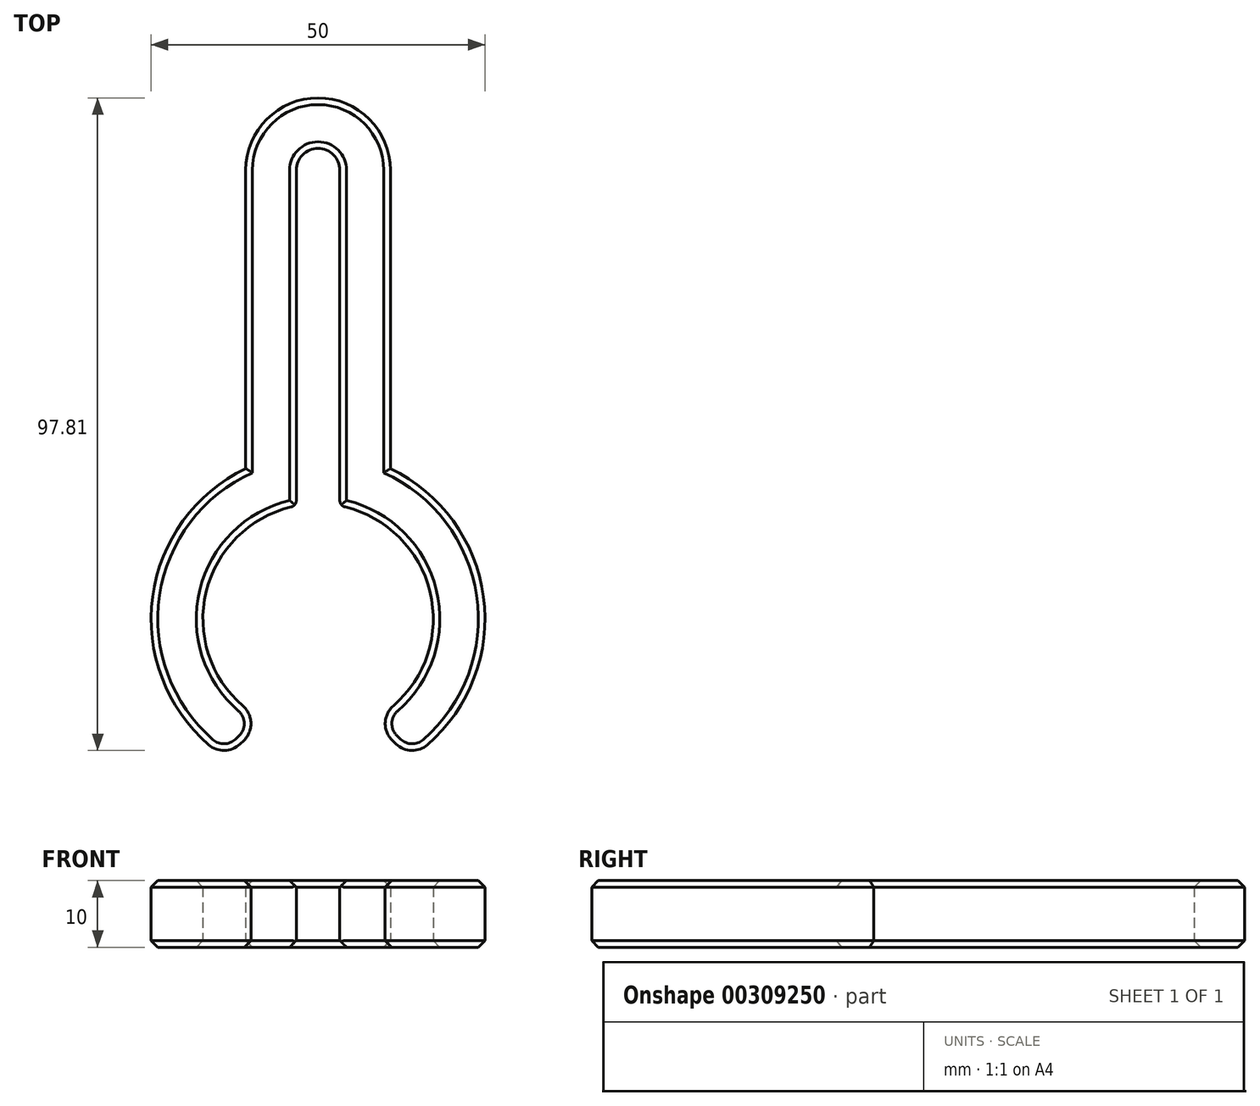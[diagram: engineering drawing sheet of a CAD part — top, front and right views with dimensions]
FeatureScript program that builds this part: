
annotation { "Feature Type Name" : "Feature", "Feature Type Description" : "" }
export const myFeature = defineFeature(function(context is Context, id is Id, definition is map)
    precondition{}
    {
        {
            var Q0;
            Q0=qCreatedBy(makeId("Top.planeOp"),FACE);
            var sketch = newSketch(context, id + "F0", { "sketchPlane" : qUnion([Q0])});
            skArc(sketch, "E0", {"start": v(-39.63, 17.45) * mm, "mid": v(-53.44, 3.03) * mm, "end": v(-44.38, -14.76) * mm});
            skArc(sketch, "E1", {"start": v(-47.2, 23.05) * mm, "mid": v(-61.31, 2.25) * mm, "end": v(-50.22, -20.3) * mm});
            skArc(sketch, "E2", {"start": v(-33.11, 67.76) * mm, "mid": v(-36.37, 71.03) * mm, "end": v(-39.63, 67.76) * mm});
            skArc(sketch, "E3", {"start": v(-25.54, 67.76) * mm, "mid": v(-36.37, 78.6) * mm, "end": v(-47.2, 67.76) * mm});
            skLineSegment(sketch, "E4", {"start": v(-25.54, 67.76) * mm, "end": v(-25.54, 23.05) * mm});
            skLineSegment(sketch, "E5", {"start": v(-47.2, 67.76) * mm, "end": v(-47.2, 23.05) * mm});
            skLineSegment(sketch, "E6", {"start": v(-33.11, 67.76) * mm, "end": v(-33.11, 17.45) * mm});
            skLineSegment(sketch, "E7", {"start": v(-39.63, 67.76) * mm, "end": v(-39.63, 17.45) * mm});
            skArc(sketch, "E8.trimOffspring", {"start": v(-28.36, -14.76) * mm, "mid": v(-19.3, 3.03) * mm, "end": v(-33.11, 17.45) * mm});
            skArc(sketch, "E9.trimOffspring", {"start": v(-22.52, -20.3) * mm, "mid": v(-11.43, 2.25) * mm, "end": v(-25.54, 23.05) * mm});
            skLineSegment(sketch, "E10", {"start": v(-50.22, -20.3) * mm, "end": v(-44.38, -14.76) * mm});
            skLineSegment(sketch, "E11", {"start": v(-28.36, -14.76) * mm, "end": v(-22.52, -20.3) * mm});
            skSolve(sketch);
        }
        {
            var Q0;
            Q0 = qSketchRegion(id + "F0", true);
            extrude(context, id + "F1", {"entities" : qUnion([Q0]), "depth" : 10 * mm});
        }
        {
            var Q0;
            Q0=makeQuery(id+"F1.opExtrude","SWEPT_EDGE",EDGE,{"disambiguationData":[OSD([sQuery(id+"F0.wireOp",EDGE,"E1"),sQuery(id+"F0.wireOp",EDGE,"E10")])]});
            var Q1;
            Q1=makeQuery(id+"F1.opExtrude","SWEPT_EDGE",EDGE,{"disambiguationData":[OSD([sQuery(id+"F0.wireOp",EDGE,"E0"),sQuery(id+"F0.wireOp",EDGE,"E10")])]});
            var Q2;
            Q2=makeQuery(id+"F1.opExtrude","SWEPT_EDGE",EDGE,{"disambiguationData":[OSD([sQuery(id+"F0.wireOp",EDGE,"E8.trimOffspring"),sQuery(id+"F0.wireOp",EDGE,"E11")])]});
            var Q3;
            Q3=makeQuery(id+"F1.opExtrude","SWEPT_EDGE",EDGE,{"disambiguationData":[OSD([sQuery(id+"F0.wireOp",EDGE,"E9.trimOffspring"),sQuery(id+"F0.wireOp",EDGE,"E11")])]});
            fillet(context, id + "F2", {"entities" : qUnion([Q0, Q1, Q2, Q3]), "radius" : 3.5 * mm, "tangentPropagation" : true, "allowEdgeOverflow" : false});
        }
        {
            var Q0;
            Q0=makeQuery(id+"F1.opExtrude","CAP_EDGE",EDGE,{"disambiguationData":[OSD([sQuery(id+"F0.wireOp",EDGE,"E0")])],"isStart":false});
            var Q1;
            Q1=makeQuery(id+"F1.opExtrude","CAP_EDGE",EDGE,{"disambiguationData":[OSD([sQuery(id+"F0.wireOp",EDGE,"leTiJdDx-6Tv0-o62X-Sqed-6rVeZV9HhB44")])],"isStart":false});
            var Q2;
            Q2=makeQuery(id+"F1.opExtrude","CAP_EDGE",EDGE,{"disambiguationData":[OSD([sQuery(id+"F0.wireOp",EDGE,"E1")])],"isStart":false});
            var Q3;
            Q3=makeQuery(id+"F1.opExtrude","CAP_EDGE",EDGE,{"disambiguationData":[OSD([sQuery(id+"F0.wireOp",EDGE,"E5")])],"isStart":false});
            var Q4;
            Q4=makeQuery(id+"F1.opExtrude","CAP_EDGE",EDGE,{"disambiguationData":[OSD([sQuery(id+"F0.wireOp",EDGE,"E7")])],"isStart":false});
            var Q5;
            Q5=makeQuery(id+"F1.opExtrude","CAP_EDGE",EDGE,{"disambiguationData":[OSD([sQuery(id+"F0.wireOp",EDGE,"E3")])],"isStart":false});
            var Q6;
            Q6=makeQuery(id+"F1.opExtrude","CAP_EDGE",EDGE,{"disambiguationData":[OSD([sQuery(id+"F0.wireOp",EDGE,"E2")])],"isStart":false});
            var Q7;
            Q7=makeQuery(id+"F1.opExtrude","CAP_EDGE",EDGE,{"disambiguationData":[OSD([sQuery(id+"F0.wireOp",EDGE,"E6")])],"isStart":false});
            var Q8;
            Q8=makeQuery(id+"F1.opExtrude","CAP_EDGE",EDGE,{"disambiguationData":[OSD([sQuery(id+"F0.wireOp",EDGE,"E4")])],"isStart":false});
            var Q9;
            Q9=makeQuery(id+"F1.opExtrude","CAP_EDGE",EDGE,{"disambiguationData":[OSD([sQuery(id+"F0.wireOp",EDGE,"E8.trimOffspring")])],"isStart":false});
            var Q10;
            Q10=makeQuery(id+"F1.opExtrude","CAP_EDGE",EDGE,{"disambiguationData":[OSD([sQuery(id+"F0.wireOp",EDGE,"E9.trimOffspring")])],"isStart":true});
            var Q11;
            Q11=makeQuery(id+"F1.opExtrude","CAP_EDGE",EDGE,{"disambiguationData":[OSD([sQuery(id+"F0.wireOp",EDGE,"E4")])],"isStart":true});
            var Q12;
            Q12=makeQuery(id+"F1.opExtrude","CAP_EDGE",EDGE,{"disambiguationData":[OSD([sQuery(id+"F0.wireOp",EDGE,"E7")])],"isStart":true});
            var Q13;
            Q13=makeQuery(id+"F1.opExtrude","CAP_EDGE",EDGE,{"disambiguationData":[OSD([sQuery(id+"F0.wireOp",EDGE,"E0")])],"isStart":true});
            chamfer(context, id + "F3", {"entities" : qUnion([Q0, Q1, Q2, Q3, Q4, Q5, Q6, Q7, Q8, Q9, Q10, Q11, Q12, Q13]), "width" : 1 * mm, "tangentPropagation" : true});
        }
        {
            var Q0;
            Q0=makeQuery(id+"F1.opExtrude","SWEPT_EDGE",EDGE,{"disambiguationData":[OSD([sQuery(id+"F0.wireOp",EDGE,"E0"),sQuery(id+"F0.wireOp",EDGE,"E7")])]});
            var Q1;
            Q1=makeQuery(id+"F1.opExtrude","SWEPT_EDGE",EDGE,{"disambiguationData":[OSD([sQuery(id+"F0.wireOp",EDGE,"E6"),sQuery(id+"F0.wireOp",EDGE,"E8.trimOffspring")])]});
            fillet(context, id + "F4", {"entities" : qUnion([Q0, Q1]), "radius" : 1 * mm, "tangentPropagation" : true, "allowEdgeOverflow" : false});
        }
    });
